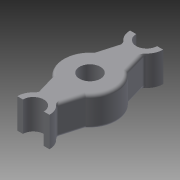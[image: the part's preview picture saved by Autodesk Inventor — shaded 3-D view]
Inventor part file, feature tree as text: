
AUTODESK INVENTOR PART (.ipt)
format: ipt  version: 2015 (Build 190159000, 159)  size: 275,968 bytes
history: native  units: in
note: dims shown in document units (in); Inventor stores cm internally (conversion verified against a paired STEP export)
features: extrude x2, fillet x2, sketch x2
ambient origin geometry x8: Origin, YZ Plane, XZ Plane, XY Plane, X Axis, Y Axis, Z Axis, Center Point
bodies: Solid1 (feature_tree)
feature tree (6):
  extrude  "Extrusion1"  Depth=14.9606in
  extrude  "Extrusion2"  Depth=2.7559in
  fillet  "Fillet1"  Radius=7.0866in
  fillet  "Fillet2"  Radius=0.7548in
  sketch  "Sketch1"  dims[d0=7.4803in d1=14.9606in]
  sketch  "Sketch2"  dims[d2=2.7559in d3=2.7559in d4=7.0866in d11=0.7548in d12=0.81in d14=3.937in d15=0.0in d16=2.7559in d17=1.9685in d18=0.0in d19=0.3937in d20=0.3937in]
